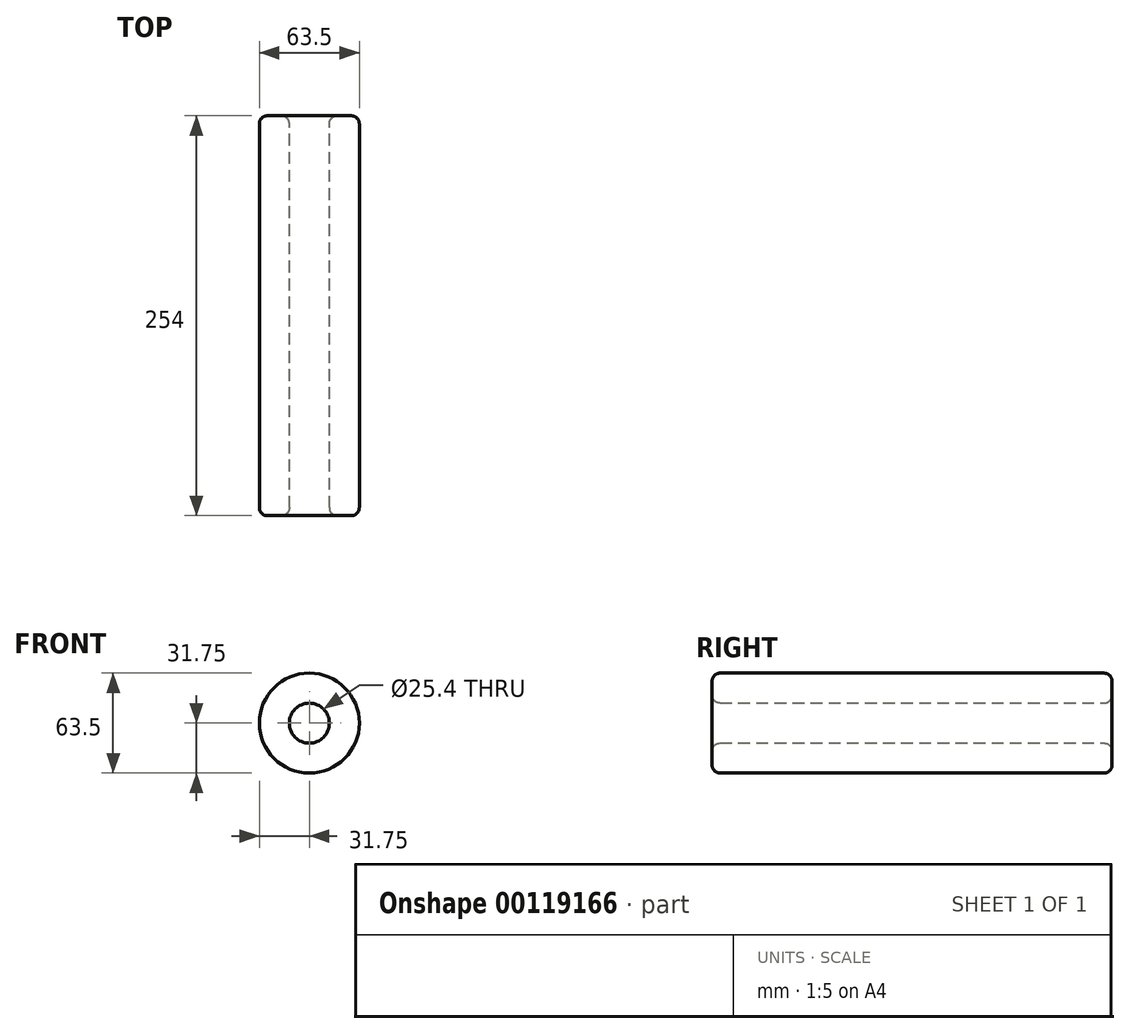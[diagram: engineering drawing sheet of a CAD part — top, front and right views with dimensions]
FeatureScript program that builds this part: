
annotation { "Feature Type Name" : "Feature", "Feature Type Description" : "" }
export const myFeature = defineFeature(function(context is Context, id is Id, definition is map)
    precondition{}
    {
        {
            var Q0;
            Q0=qCreatedBy(makeId("Front.planeOp"),FACE);
            var sketch = newSketch(context, id + "F0", { "sketchPlane" : qUnion([Q0])});
            skCircle(sketch, "E0", {"center": v(0, 0) * mm, "radius": 31.75 * mm});
            skSolve(sketch);
        }
        {
            var Q0;
            Q0 = qSketchRegion(id + "F0", true);
            extrude(context, id + "F1", {"entities" : qUnion([Q0]), "depth" : 254 * mm});
        }
        {
            var Q0;
            Q0=makeQuery(id+"F1.opExtrude","CAP_EDGE",EDGE,{"disambiguationData":[OSD([sQuery(id+"F0.wireOp",EDGE,"E0")])],"isStart":false});
            fillet(context, id + "F2", {"entities" : qUnion([Q0]), "radius" : 5.08 * mm, "tangentPropagation" : true, "allowEdgeOverflow" : false});
        }
        {
            var Q0;
            Q0=makeQuery(id+"F1.opExtrude","CAP_EDGE",EDGE,{"disambiguationData":[OSD([sQuery(id+"F0.wireOp",EDGE,"E0")])],"isStart":true});
            fillet(context, id + "F3", {"entities" : qUnion([Q0]), "radius" : 5.08 * mm, "tangentPropagation" : true, "allowEdgeOverflow" : false});
        }
        {
            var Q0;
            Q0=makeQuery(id+"F1.opExtrude","CAP_FACE",FACE,{"disambiguationData":[OSD([sQuery(id+"F0.wireOp",EDGE,"E0")])],"isStart":true});
            var sketch = newSketch(context, id + "F4", { "sketchPlane" : qUnion([Q0])});
            skCircle(sketch, "E1", {"center": v(0, 0) * mm, "radius": 12.7 * mm});
            skSolve(sketch);
        }
        {
            var Q0;
            Q0 = qSketchRegion(id + "F4", true);
            extrude(context, id + "F5", {"entities" : qUnion([Q0]), "operationType" : NewBodyOperationType.REMOVE, "endBound" : BoundingType.THROUGH_ALL, "oppositeDirection" : true, "depth" : 25.4 * mm});
        }
        {
            var Q0;
            Q0=makeQuery(id+"F5.boolean.opBoolean","COPY",FACE,{"derivedFrom":makeQuery(id+"F5.opExtrude","SWEPT_FACE",FACE,{"disambiguationData":[OSD([sQuery(id+"F4.wireOp",EDGE,"E1")])]})});
            fillet(context, id + "F6", {"entities" : qUnion([Q0]), "radius" : 5.08 * mm, "tangentPropagation" : true, "allowEdgeOverflow" : false});
        }
    });
